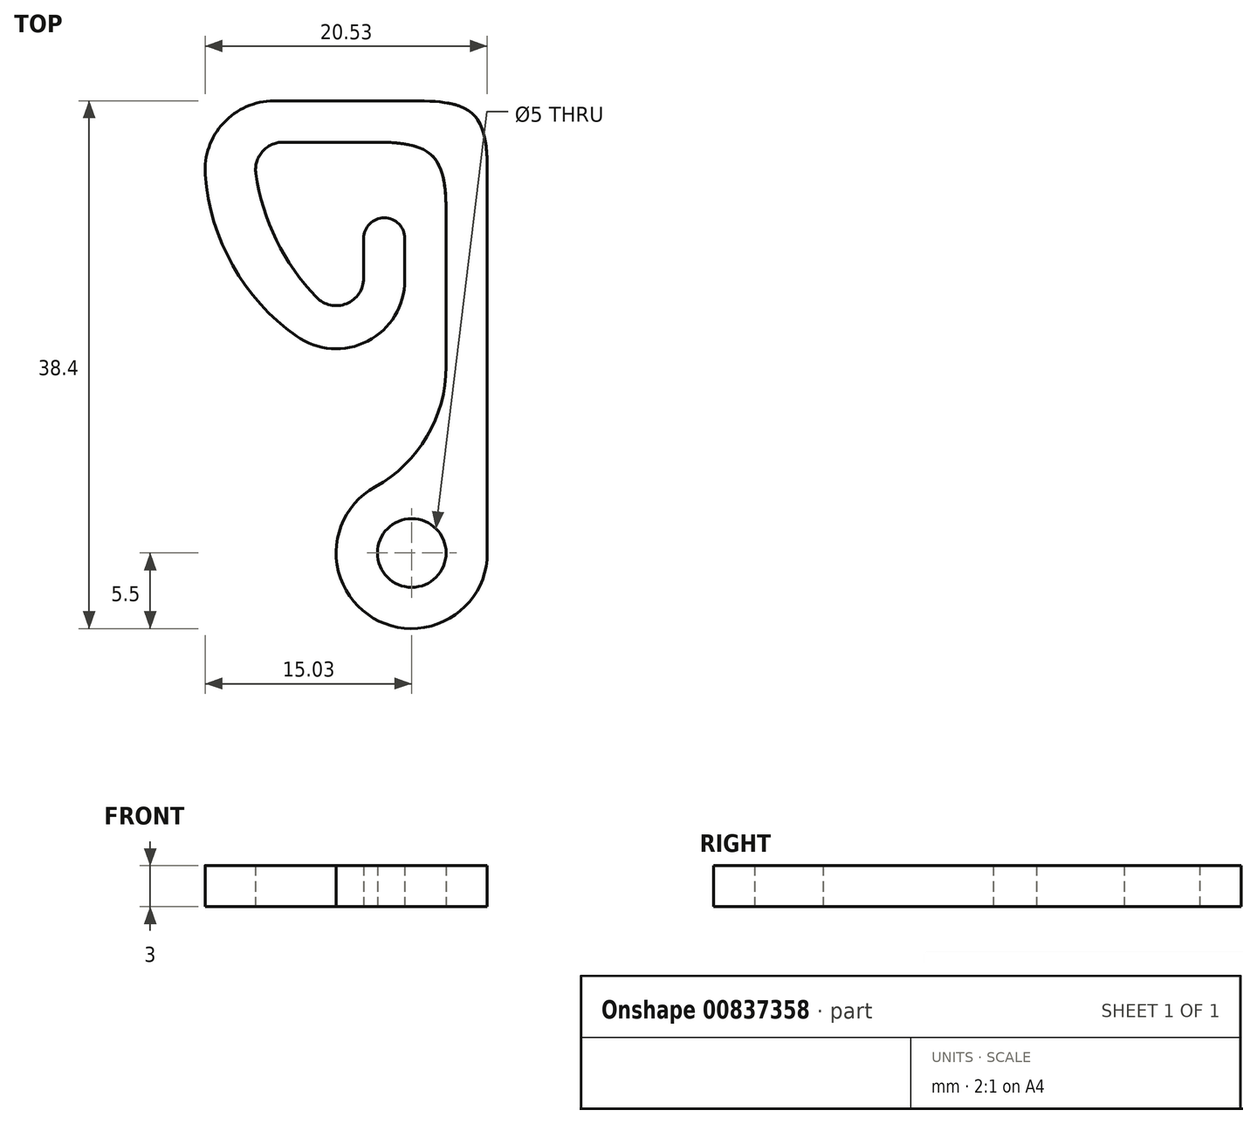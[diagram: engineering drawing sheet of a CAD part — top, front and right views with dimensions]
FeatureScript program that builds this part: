
annotation { "Feature Type Name" : "Feature", "Feature Type Description" : "" }
export const myFeature = defineFeature(function(context is Context, id is Id, definition is map)
    precondition{}
    {
        {
            var Q0;
            Q0=qCreatedBy(makeId("Top.planeOp"),FACE);
            var sketch = newSketch(context, id + "F0", { "sketchPlane" : qUnion([Q0])});
            skCircle(sketch, "E0", {"center": v(0, 0) * mm, "radius": 2.5 * mm});
            skCircle(sketch, "E1", {"center": v(0, 0) * mm, "radius": 5.5 * mm});
            skLineSegment(sketch, "E2", {"start": v(5.5, 0) * mm, "end": v(5.5, 32.9) * mm});
            skLineSegment(sketch, "E3", {"start": v(5.5, 32.9) * mm, "end": v(-14.5, 32.9) * mm});
            skLineSegment(sketch, "E4", {"start": v(-14.5, 32.9) * mm, "end": v(-14.5, 12.9) * mm});
            skLineSegment(sketch, "E5", {"start": v(-14.5, 12.9) * mm, "end": v(-0.5, 12.9) * mm});
            skLineSegment(sketch, "E6", {"start": v(-0.5, 12.9) * mm, "end": v(-0.5, 22.9) * mm});
            skLineSegment(sketch, "E7.0", {"start": v(-3.5, 15.9) * mm, "end": v(-3.5, 22.9) * mm});
            skLineSegment(sketch, "E7.1", {"start": v(2.5, 0) * mm, "end": v(2.5, 29.9) * mm});
            skLineSegment(sketch, "E7.2", {"start": v(2.5, 29.9) * mm, "end": v(-11.5, 29.9) * mm});
            skLineSegment(sketch, "E7.3", {"start": v(-11.5, 29.9) * mm, "end": v(-11.5, 15.9) * mm});
            skLineSegment(sketch, "E7.4", {"start": v(-11.5, 15.9) * mm, "end": v(-3.5, 15.9) * mm});
            skArc(sketch, "E8", {"start": v(-0.5, 22.9) * mm, "mid": v(-2, 24.4) * mm, "end": v(-3.5, 22.9) * mm});
            skPoint(sketch, "E9", {"position": v(2.5, 4.9) * mm});
            skArc(sketch, "E10", {"start": v(-11.5, 29.9) * mm, "mid": v(-9.36, 21.84) * mm, "end": v(-3.5, 15.9) * mm});
            skArc(sketch, "E11", {"start": v(-14.5, 32.9) * mm, "mid": v(-12.2, 19.61) * mm, "end": v(-0.5, 12.9) * mm});
            skSolve(sketch);
        }
        {
            var Q0;
            {var subQ4=sQuery(id+"F0.wireOp",EDGE,"E2");Q0=makeQuery(id+"F0.imprint","IMPRINT",FACE,{"disambiguationData":[TD([[makeQuery(id+"F0.imprint","IMPRINT",EDGE,{"derivedFrom":subQ4}),1.0]])]});}
            var Q1;
            Q1=makeQuery(id+"F0.imprint","IMPRINT",FACE,{"disambiguationData":[TD([[makeQuery(id+"F0.imprint","IMPRINT",EDGE,{"derivedFrom":sQuery(id+"F0.wireOp",EDGE,"E0")}),-1.0]])]});
            var Q2;
            {var subQ0=sQuery(id+"F0.wireOp",EDGE,"E10");Q2=makeQuery(id+"F0.imprint","IMPRINT",FACE,{"disambiguationData":[TD([[makeQuery(id+"F0.imprint","IMPRINT",EDGE,{"derivedFrom":subQ0}),-1.0]])]});}
            var Q3;
            {var subQ4=sQuery(id+"F0.wireOp",EDGE,"E6");Q3=makeQuery(id+"F0.imprint","IMPRINT",FACE,{"disambiguationData":[TD([[makeQuery(id+"F0.imprint","IMPRINT",EDGE,{"derivedFrom":subQ4}),1.0]])]});}
            var Q4;
            {var subQ0=sQuery(id+"F0.wireOp",EDGE,"E11");var subQ1=sQuery(id+"F0.wireOp",EDGE,"E4");var subQ3=makeQuery(id+"F0.imprint","INTERSECT",VERTEX,{"derivedFrom":[subQ1,subQ0]});Q4=makeQuery(id+"F0.imprint","IMPRINT",FACE,{"disambiguationData":[TD([[makeQuery(id+"F0.imprint","IMPRINT",EDGE,{"disambiguationData":[TD([[subQ3,1.0]])],"derivedFrom":subQ1}),-1.0]])]});}
            extrude(context, id + "F1", {"entities" : qUnion([Q0, Q1, Q2, Q3, Q4]), "depth" : 3 * mm, "offsetDistance" : 25 * mm});
        }
        {
            var Q0;
            Q0=makeQuery(id+"F1.opExtrude","SWEPT_EDGE",EDGE,{"disambiguationData":[OSD([sQuery(id+"F0.wireOp",EDGE,"E7.0"),sQuery(id+"F0.wireOp",EDGE,"E7.4"),sQuery(id+"F0.wireOp",EDGE,"E10")])]});
            fillet(context, id + "F2", {"entities" : qUnion([Q0]), "radius" : 2 * mm, "tangentPropagation" : true, "allowEdgeOverflow" : false});
        }
        {
            var Q0;
            Q0=makeQuery(id+"F1.opExtrude","SWEPT_EDGE",EDGE,{"disambiguationData":[OSD([sQuery(id+"F0.wireOp",EDGE,"E2"),sQuery(id+"F0.wireOp",EDGE,"E3")])]});
            var Q1;
            Q1=makeQuery(id+"F1.opExtrude","SWEPT_EDGE",EDGE,{"disambiguationData":[OSD([sQuery(id+"F0.wireOp",EDGE,"E7.1"),sQuery(id+"F0.wireOp",EDGE,"E7.2")])]});
            fillet(context, id + "F3", {"entities" : qUnion([Q0, Q1]), "radius" : 5 * mm, "tangentPropagation" : true, "rho" : .6, "crossSection" : FilletCrossSection.CONIC, "allowEdgeOverflow" : false});
        }
        {
            var Q0;
            Q0=makeQuery(id+"F1.opExtrude","SWEPT_EDGE",EDGE,{"disambiguationData":[OSD([sQuery(id+"F0.wireOp",EDGE,"E1"),sQuery(id+"F0.wireOp",EDGE,"E7.1")])]});
            fillet(context, id + "F4", {"entities" : qUnion([Q0]), "radius" : 10 * mm, "tangentPropagation" : true, "allowEdgeOverflow" : false});
        }
        {
            var Q0;
            Q0=makeQuery(id+"F1.opExtrude","SWEPT_EDGE",EDGE,{"disambiguationData":[OSD([sQuery(id+"F0.wireOp",EDGE,"E5"),sQuery(id+"F0.wireOp",EDGE,"E6"),sQuery(id+"F0.wireOp",EDGE,"E11")])]});
            fillet(context, id + "F5", {"entities" : qUnion([Q0]), "radius" : 5 * mm, "tangentPropagation" : true, "allowEdgeOverflow" : false});
        }
        {
            var Q0;
            Q0=makeQuery(id+"F1.opExtrude","SWEPT_EDGE",EDGE,{"disambiguationData":[OSD([sQuery(id+"F0.wireOp",EDGE,"E3"),sQuery(id+"F0.wireOp",EDGE,"E4"),sQuery(id+"F0.wireOp",EDGE,"E11")])]});
            fillet(context, id + "F6", {"entities" : qUnion([Q0]), "radius" : 5 * mm, "tangentPropagation" : true, "allowEdgeOverflow" : false});
        }
        {
            var Q0;
            Q0=makeQuery(id+"F1.opExtrude","SWEPT_EDGE",EDGE,{"disambiguationData":[OSD([sQuery(id+"F0.wireOp",EDGE,"E7.2"),sQuery(id+"F0.wireOp",EDGE,"E7.3"),sQuery(id+"F0.wireOp",EDGE,"E10")])]});
            fillet(context, id + "F7", {"entities" : qUnion([Q0]), "radius" : 2 * mm, "tangentPropagation" : true, "allowEdgeOverflow" : false});
        }
    });
